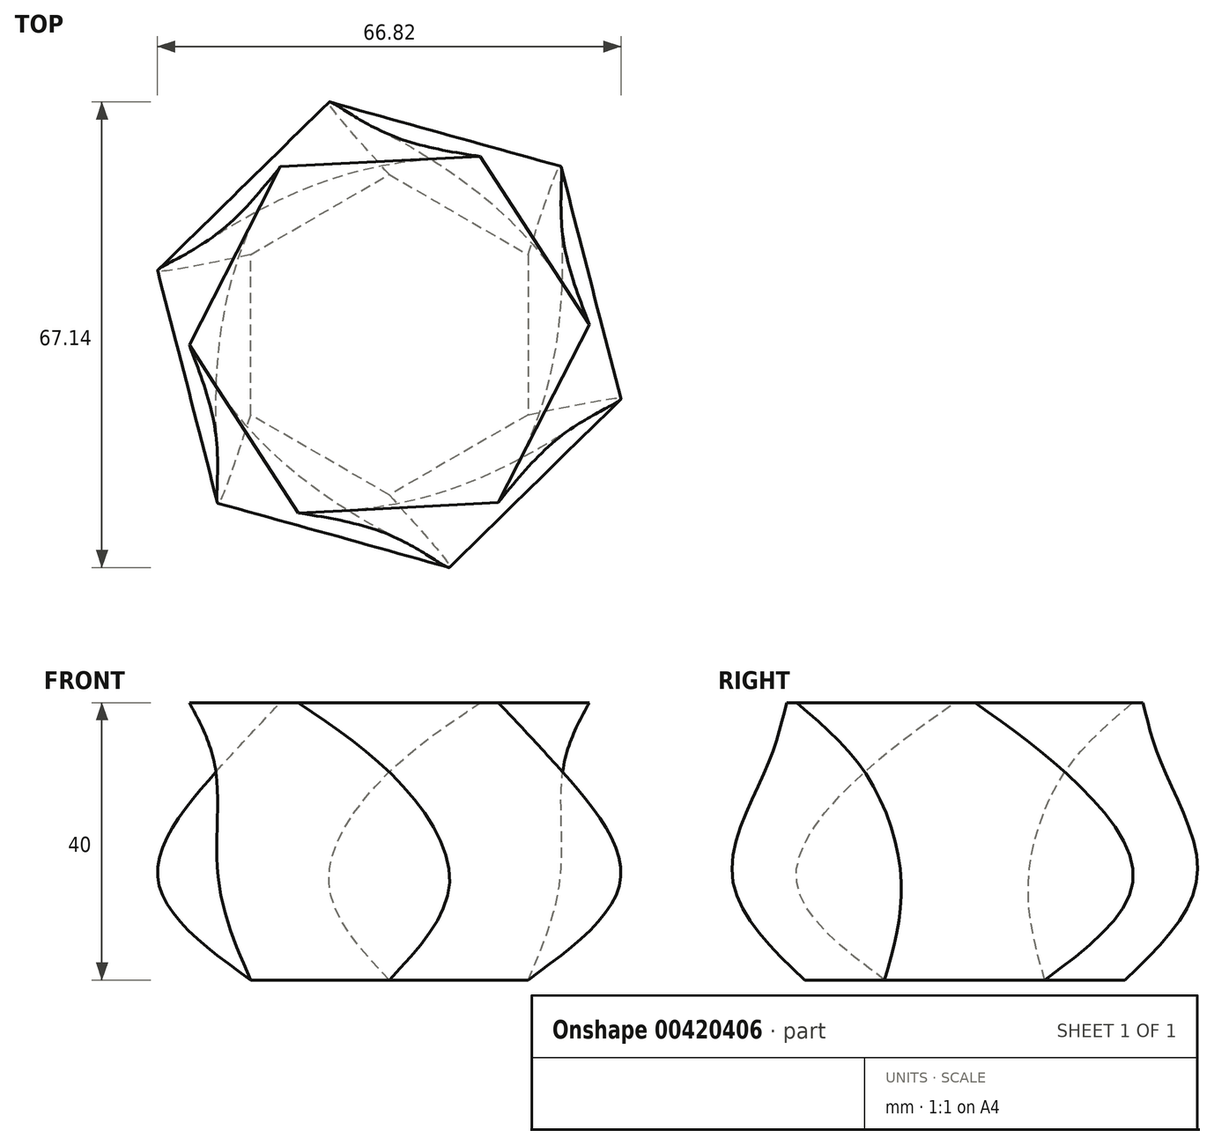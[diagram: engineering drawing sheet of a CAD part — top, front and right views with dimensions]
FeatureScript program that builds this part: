
annotation { "Feature Type Name" : "Feature", "Feature Type Description" : "" }
export const myFeature = defineFeature(function(context is Context, id is Id, definition is map)
    precondition{}
    {
        {
            var Q0;
            Q0=qCreatedBy(makeId("Top.planeOp"),FACE);
            var sketch = newSketch(context, id + "F0", { "sketchPlane" : qUnion([Q0])});
            skPoint(sketch, "E0.0.midPoint", {"position": v(20, 0) * mm});
            skLineSegment(sketch, "E1", {"start": v(20, 0) * mm, "end": v(-20, 0) * mm, "construction": true});
            skCircle(sketch, "E2.cCircle", {"center": v(0, 0) * mm, "radius": 20 * mm, "construction": true});
            skLineSegment(sketch, "E2.0", {"start": v(20, 11.55) * mm, "end": v(20, -11.55) * mm});
            skLineSegment(sketch, "E2.1", {"start": v(20, -11.55) * mm, "end": v(0, -23.1) * mm});
            skLineSegment(sketch, "E2.2", {"start": v(0, -23.1) * mm, "end": v(-20, -11.55) * mm});
            skLineSegment(sketch, "E2.3", {"start": v(-20, -11.55) * mm, "end": v(-20, 11.55) * mm});
            skLineSegment(sketch, "E2.4", {"start": v(-20, 11.55) * mm, "end": v(0, 23.1) * mm});
            skLineSegment(sketch, "E2.5", {"start": v(0, 23.1) * mm, "end": v(20, 11.55) * mm});
            skLineSegment(sketch, "E3", {"start": v(0, 20) * mm, "end": v(0, -20) * mm, "construction": true});
            skSolve(sketch);
        }
        {
            var Q0;
            Q0=qCreatedBy(makeId("Top.planeOp"),FACE);
            cPlane(context, id + "F1", {"entities" : qUnion([Q0]), "cplaneType" : CPlaneType.OFFSET, "offset" : 15 * mm, "width" : 150 * mm, "height" : 150 * mm});
        }
        {
            var Q0;
            Q0=qCreatedBy(id+"F1.planeOp",FACE);
            var sketch = newSketch(context, id + "F2", { "sketchPlane" : qUnion([Q0])});
            skLineSegment(sketch, "E4.0", {"start": v(20, 0) * mm, "end": v(-20, 0) * mm, "construction": true});
            skLineSegment(sketch, "E4.1", {"start": v(0, 20) * mm, "end": v(0, -20) * mm, "construction": true});
            skPoint(sketch, "E4.2", {"position": v(0, 0) * mm});
            skLineSegment(sketch, "E5", {"start": v(-14.14, 14.14) * mm, "end": v(14.14, -14.14) * mm, "construction": true});
            skCircle(sketch, "E6.cCircle", {"center": v(0, 0) * mm, "radius": 30 * mm, "construction": true});
            skLineSegment(sketch, "E6.0", {"start": v(-33.4, 9.22) * mm, "end": v(-8.7, 33.53) * mm});
            skLineSegment(sketch, "E6.1", {"start": v(-8.7, 33.53) * mm, "end": v(24.68, 24.3) * mm});
            skLineSegment(sketch, "E6.2", {"start": v(24.68, 24.3) * mm, "end": v(33.4, -9.22) * mm});
            skLineSegment(sketch, "E6.3", {"start": v(33.4, -9.22) * mm, "end": v(8.7, -33.53) * mm});
            skLineSegment(sketch, "E6.4", {"start": v(8.7, -33.53) * mm, "end": v(-24.68, -24.3) * mm});
            skLineSegment(sketch, "E6.5", {"start": v(-24.68, -24.3) * mm, "end": v(-33.4, 9.22) * mm});
            skPoint(sketch, "E6.0.midPoint", {"position": v(-21.05, 21.38) * mm});
            skSolve(sketch);
        }
        {
            var Q0;
            Q0=qCreatedBy(id+"F1.planeOp",FACE);
            cPlane(context, id + "F3", {"entities" : qUnion([Q0]), "cplaneType" : CPlaneType.OFFSET, "offset" : 15 * mm, "width" : 150 * mm, "height" : 150 * mm});
        }
        {
            var Q0;
            Q0=qCreatedBy(id+"F3.planeOp",FACE);
            var sketch = newSketch(context, id + "F4", { "sketchPlane" : qUnion([Q0])});
            skLineSegment(sketch, "E7.0", {"start": v(0, 20) * mm, "end": v(0, -20) * mm, "construction": true});
            skLineSegment(sketch, "E7.1", {"start": v(20, 0) * mm, "end": v(-20, 0) * mm, "construction": true});
            skPoint(sketch, "E7.2", {"position": v(0, 0) * mm});
            skCircle(sketch, "E8.cCircle", {"center": v(0, 0) * mm, "radius": 25 * mm, "construction": true});
            skLineSegment(sketch, "E8.0", {"start": v(25, 14.43) * mm, "end": v(25, -14.43) * mm});
            skLineSegment(sketch, "E8.1", {"start": v(25, -14.43) * mm, "end": v(0, -28.87) * mm});
            skLineSegment(sketch, "E8.2", {"start": v(0, -28.87) * mm, "end": v(-25, -14.43) * mm});
            skLineSegment(sketch, "E8.3", {"start": v(-25, -14.43) * mm, "end": v(-25, 14.43) * mm});
            skLineSegment(sketch, "E8.4", {"start": v(-25, 14.43) * mm, "end": v(0, 28.87) * mm});
            skLineSegment(sketch, "E8.5", {"start": v(0, 28.87) * mm, "end": v(25, 14.43) * mm});
            skPoint(sketch, "E8.0.midPoint", {"position": v(0, -25) * mm});
            skSolve(sketch);
        }
        {
            var Q0;
            Q0=makeQuery(id+"F4.imprint","IMPRINT",FACE,{"disambiguationData":[TD([[makeQuery(id+"F4.imprint","IMPRINT",EDGE,{"derivedFrom":sQuery(id+"F4.wireOp",EDGE,"E8.0")}),-1.0]])]});
            cPlane(context, id + "F5", {"entities" : qUnion([Q0]), "cplaneType" : CPlaneType.OFFSET, "offset" : 10 * mm, "width" : 150 * mm, "height" : 150 * mm});
        }
        {
            var Q0;
            Q0=qCreatedBy(id+"F5.planeOp",FACE);
            var sketch = newSketch(context, id + "F6", { "sketchPlane" : qUnion([Q0])});
            skLineSegment(sketch, "E9.0", {"start": v(0, 20) * mm, "end": v(0, -20) * mm, "construction": true});
            skLineSegment(sketch, "E9.1", {"start": v(20, 0) * mm, "end": v(-20, 0) * mm, "construction": true});
            skPoint(sketch, "E9.2", {"position": v(0, 0) * mm});
            skCircle(sketch, "E10.cCircle", {"center": v(0, 0) * mm, "radius": 25 * mm, "construction": true});
            skLineSegment(sketch, "E10.0", {"start": v(-15.7, 24.23) * mm, "end": v(13.13, 25.7) * mm});
            skLineSegment(sketch, "E10.1", {"start": v(13.13, 25.7) * mm, "end": v(28.83, 1.48) * mm});
            skLineSegment(sketch, "E10.2", {"start": v(28.83, 1.48) * mm, "end": v(15.7, -24.23) * mm});
            skLineSegment(sketch, "E10.3", {"start": v(15.7, -24.23) * mm, "end": v(-13.13, -25.7) * mm});
            skLineSegment(sketch, "E10.4", {"start": v(-13.13, -25.7) * mm, "end": v(-28.83, -1.48) * mm});
            skLineSegment(sketch, "E10.5", {"start": v(-28.83, -1.48) * mm, "end": v(-15.7, 24.23) * mm});
            skPoint(sketch, "E10.0.midPoint", {"position": v(0, 25) * mm});
            skSolve(sketch);
        }
        {
            var Q0;
            Q0=makeQuery(id+"F0.imprint","IMPRINT",FACE,{"disambiguationData":[TD([[makeQuery(id+"F0.imprint","IMPRINT",EDGE,{"derivedFrom":sQuery(id+"F0.wireOp",EDGE,"E2.0")}),-1.0]])]});
            var Q1;
            Q1=makeQuery(id+"F2.imprint","IMPRINT",FACE,{"disambiguationData":[TD([[makeQuery(id+"F2.imprint","IMPRINT",EDGE,{"derivedFrom":sQuery(id+"F2.wireOp",EDGE,"E6.0")}),-1.0]])]});
            var Q2;
            Q2=makeQuery(id+"F4.imprint","IMPRINT",FACE,{"disambiguationData":[TD([[makeQuery(id+"F4.imprint","IMPRINT",EDGE,{"derivedFrom":sQuery(id+"F4.wireOp",EDGE,"E8.0")}),-1.0]])]});
            var Q3;
            Q3=makeQuery(id+"F6.imprint","IMPRINT",FACE,{"disambiguationData":[TD([[makeQuery(id+"F6.imprint","IMPRINT",EDGE,{"derivedFrom":sQuery(id+"F6.wireOp",EDGE,"E10.0")}),-1.0]])]});
            loft(context, id + "F7", {"sheetProfilesArray" : [{ "sheetProfileEntities" : qUnion([Q0]) }, { "sheetProfileEntities" : qUnion([Q1]) }, { "sheetProfileEntities" : qUnion([Q2]) }, { "sheetProfileEntities" : qUnion([Q3]) }]});
        }
    });
